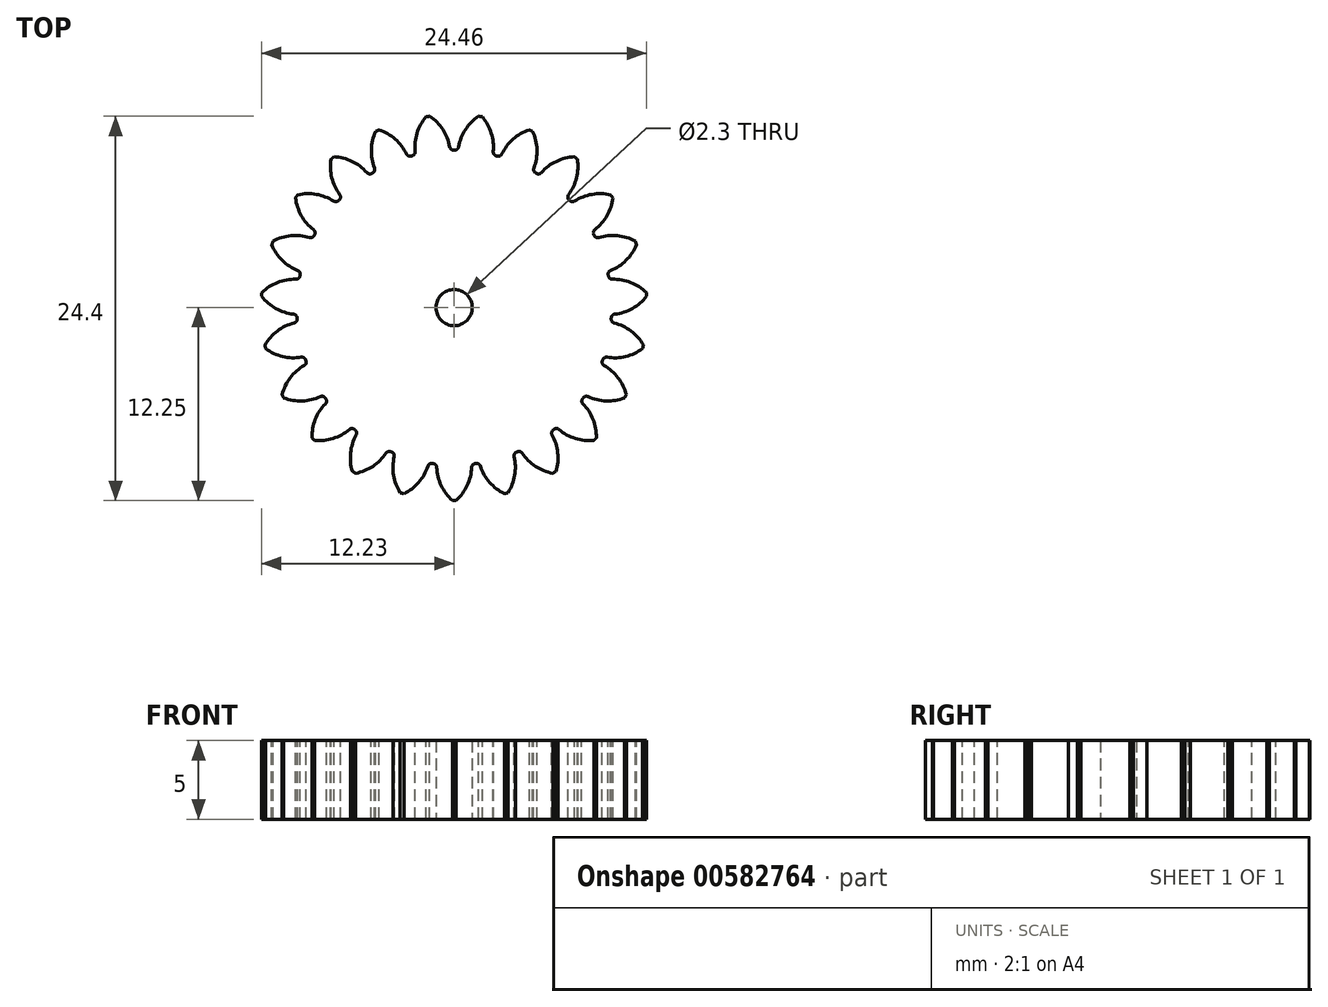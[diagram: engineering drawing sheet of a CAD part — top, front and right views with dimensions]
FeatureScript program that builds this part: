
annotation { "Feature Type Name" : "Feature", "Feature Type Description" : "" }
export const myFeature = defineFeature(function(context is Context, id is Id, definition is map)
    precondition{}
    {
        {
            var Q0;
            Q0=qCreatedBy(makeId("Top.planeOp"),FACE);
            var sketch = newSketch(context, id + "F0", { "sketchPlane" : qUnion([Q0])});
            skCircle(sketch, "E0", {"center": v(0, 0) * mm, "radius": 12.25 * mm});
            skCircle(sketch, "E1", {"center": v(0, 0) * mm, "radius": 1.15 * mm});
            skSolve(sketch);
        }
        {
            var Q0;
            Q0=qSketchRegion(id+"F0",true);
            extrude(context, id + "F1", {"entities" : qUnion([Q0]), "depth" : 5 * mm});
        }
        {
            var Q0;
            Q0=makeQuery(id+"F1.opExtrude","CAP_FACE",FACE,{"disambiguationData":[OSD([sQuery(id+"F0.wireOp",EDGE,"E0"),sQuery(id+"F0.wireOp",EDGE,"E1")])],"isStart":false});
            var sketch = newSketch(context, id + "F2", { "sketchPlane" : qUnion([Q0])});
            skArc(sketch, "E2", {"start": v(1.55, 12.15) * mm, "mid": v(0, 12.25) * mm, "end": v(-1.55, 12.15) * mm});
            skArc(sketch, "E3", {"start": v(0.03, 10) * mm, "mid": v(0, 10) * mm, "end": v(-0.03, 10) * mm});
            skArc(sketch, "E4", {"start": v(-0.28, 10.2) * mm, "mid": v(-0.72, 11.3) * mm, "end": v(-1.55, 12.15) * mm});
            skArc(sketch, "E5.MirrorCS", {"start": v(0.28, 10.2) * mm, "mid": v(0.72, 11.3) * mm, "end": v(1.55, 12.15) * mm});
            skPoint(sketch, "E6.visualSharp", {"position": v(0.25, 10) * mm});
            skArc(sketch, "E6.filletArc", {"start": v(0.03, 10) * mm, "mid": v(0.2, 10.06) * mm, "end": v(0.28, 10.2) * mm});
            skPoint(sketch, "E7.visualSharp", {"position": v(-0.25, 10) * mm});
            skArc(sketch, "E7.filletArc", {"start": v(-0.28, 10.2) * mm, "mid": v(-0.2, 10.06) * mm, "end": v(-0.03, 10) * mm});
            skSolve(sketch);
        }
        {
            var Q0;
            {var subQ0=sQuery(id+"F2.wireOp",EDGE,"E4");Q0=makeQuery(id+"F2.imprint","IMPRINT",FACE,{"disambiguationData":[TD([[makeQuery(id+"F2.imprint","IMPRINT",EDGE,{"derivedFrom":subQ0}),-1.0]])]});}
            extrude(context, id + "F3", {"entities" : qUnion([Q0]), "operationType" : NewBodyOperationType.REMOVE, "oppositeDirection" : true, "depth" : 25 * mm});
        }
        {
            var Q0;
            Q0=makeQuery(id+"F3.boolean.opBoolean","COPY",FACE,{"derivedFrom":makeQuery(id+"F3.opExtrude","SWEPT_FACE",FACE,{"disambiguationData":[OSD([sQuery(id+"F2.wireOp",EDGE,"E4")])]})});
            var Q1;
            Q1=makeQuery(id+"F3.boolean.opBoolean","COPY",FACE,{"derivedFrom":makeQuery(id+"F3.opExtrude","SWEPT_FACE",FACE,{"disambiguationData":[OSD([sQuery(id+"F2.wireOp",EDGE,"E7.filletArc")])]})});
            var Q2;
            Q2=makeQuery(id+"F3.boolean.opBoolean","COPY",FACE,{"derivedFrom":makeQuery(id+"F3.opExtrude","SWEPT_FACE",FACE,{"disambiguationData":[OSD([sQuery(id+"F2.wireOp",EDGE,"E3")])]})});
            var Q3;
            Q3=makeQuery(id+"F3.boolean.opBoolean","COPY",FACE,{"derivedFrom":makeQuery(id+"F3.opExtrude","SWEPT_FACE",FACE,{"disambiguationData":[OSD([sQuery(id+"F2.wireOp",EDGE,"E6.filletArc")])]})});
            var Q4;
            Q4=makeQuery(id+"F3.boolean.opBoolean","COPY",FACE,{"derivedFrom":makeQuery(id+"F3.opExtrude","SWEPT_FACE",FACE,{"disambiguationData":[OSD([sQuery(id+"F2.wireOp",EDGE,"E5.MirrorCS")])]})});
            var Q5;
            Q5=makeQuery(id+"F1.opExtrude","SWEPT_FACE",FACE,{"disambiguationData":[OSD([sQuery(id+"F0.wireOp",EDGE,"E0")])]});
            circularPattern(context, id + "F4", {"patternType" : PatternType.FACE, "faces" : qUnion([Q0, Q1, Q2, Q3, Q4]), "axis" : qUnion([Q5]), "angle" : 360 * degree, "instanceCount" : 23, "equalSpace" : true});
        }
    });
